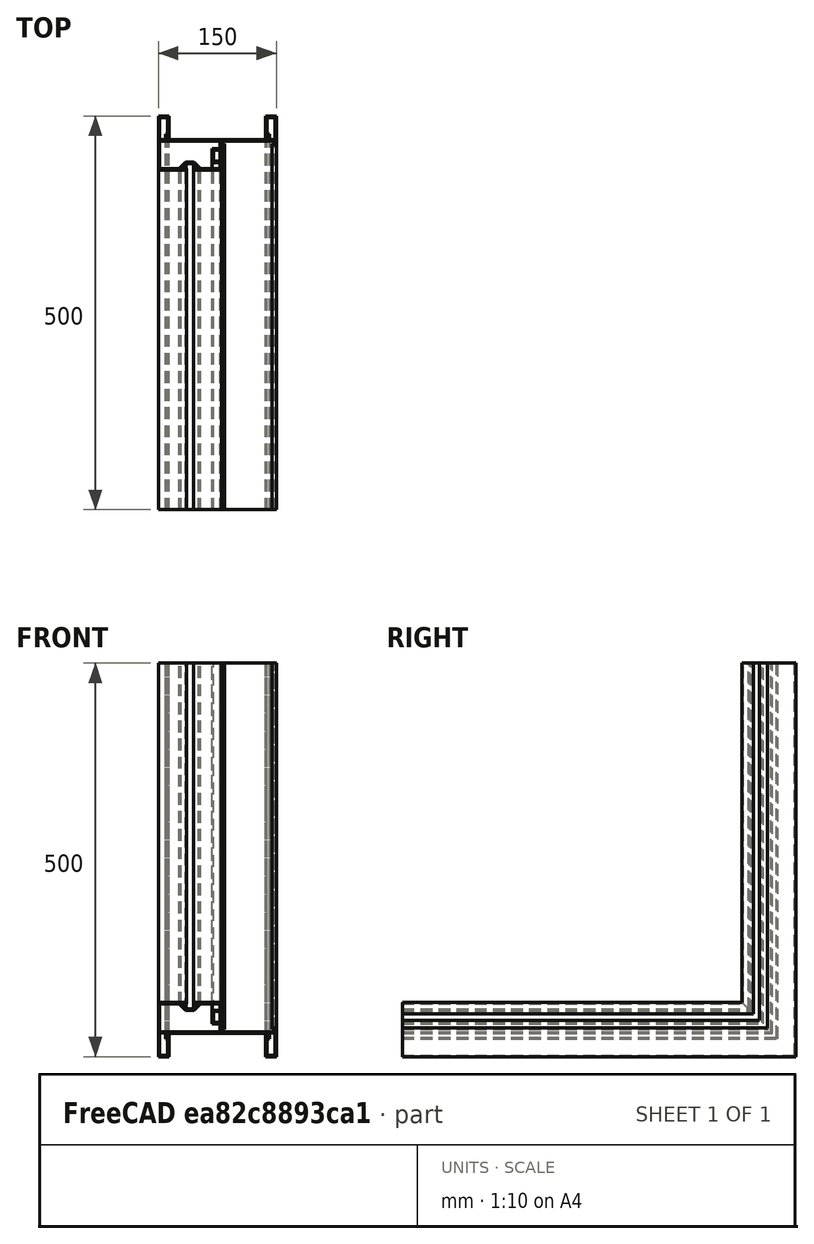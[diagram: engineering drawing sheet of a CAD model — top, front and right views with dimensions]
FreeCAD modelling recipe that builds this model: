
FCSTD DOCUMENT  (FreeCAD 0.20R24893 (Git))
Label: Profile_stripped
License: All rights reserved
LicenseURL: http://en.wikipedia.org/wiki/All_rights_reserved
objects: Part::Feature×5, Part::FeaturePython×4, Part::Face×1, Part::Extrusion×1, Fem::FemSolverObjectPython×1, App::MaterialObjectPython×1, PartDesign::Plane×1, Fem::ConstraintFixed×1, Fem::ConstraintForce×1, Part::MultiFuse×1, Fem::FemMeshObjectPython×1, Fem::FemAnalysis×1
note: 13 computed .brp shape members not serialized (recipe doc carries the construction recipe); baked Part::Feature solids carry a one-line shape summary decoded from their .brp

FEATURE [Part::Feature] Shape
  shape: bbox 150 x 68.8 x 2e-07 mm, 0 faces, 0 solids (baked)
FEATURE [Part::Feature] Shape001
  shape: bbox 10.2 x 28.2 x 2e-07 mm, 0 faces, 0 solids (baked)
FEATURE [Part::Feature] Shape002
  shape: bbox 76.4 x 35.2 x 2e-07 mm, 0 faces, 0 solids (baked)
FEATURE [Part::Feature] Shape003
  shape: bbox 10.2 x 28.2 x 2e-07 mm, 0 faces, 0 solids (baked)
FEATURE [Part::Face] Face
  FaceMakerClass = Part::FaceMakerBullseye
  Sources = -> [Shape003,Shape002,Shape001,Shape]
FEATURE [Part::Extrusion] Extrude
  Base = -> Face
  Dir = (0,0,1)
  DirMode = 2
  FaceMakerClass = Part::FaceMakerBullseye
  LengthFwd = 500
  LengthRev = 0
  Placement = pos=(0,-68.8,0) rot=(0,0,1;0rad)
  Solid = false
  Symmetric = false
FEATURE [Fem::FemSolverObjectPython] SolverCcxTools  # FEM object (typed FeaturePython)
  AnalysisType = 0
  BeamShellResultOutput3D = false
  EigenmodeHighLimit = 1000000
  EigenmodeLowLimit = 0
  EigenmodesCount = 10
  GeometricalNonlinearity = 0
  IterationsControlParameterCutb = 0.25,0.5,0.75,0.85,,,1.5,
  IterationsControlParameterIter = 4,8,9,200,10,400,,200,,
  IterationsControlParameterTimeUse = false
  IterationsThermoMechMaximum = 2000
  IterationsUserDefinedIncrementations = false
  IterationsUserDefinedTimeStepLength = false
  MaterialNonlinearity = 0
  MatrixSolverType = 0
  SplitInputWriter = false
  ThermoMechSteadyState = true
  TimeEnd = 1
  TimeInitialStep = 0.01
FEATURE [App::MaterialObjectPython] MaterialSolid  # material (typed FeaturePython)
  Category = 0
  Material = AuthorAndLicense=CalculiX-Steel,CardName=CalculiX-Steel,Density=7900 kg/m^3,Description=Standard steel material for CalculiX sample calculations,+7 more (map truncated)
FEATURE [Part::Feature] Extrude001  label="ExtrudeCopy"
  Placement = pos=(0,-500,68.8) rot=(-1,0,0;1.5708rad)
  shape: bbox 150 x 500 x 68.8 mm, 64 faces (baked)
FEATURE [PartDesign::Plane] PartDesign__Plane002
  AttachmentOffset = pos=(0,0,0) rot=(-1,0,0;0.785398rad)
  Length = 259.59
  MapMode = 49
  Placement = pos=(0,1.53e-14,3.411e-13) rot=(-1,0,0;0.785398rad)
  ResizeMode = 0
  Support = -> [Extrude001]
  Width = 838.26
FEATURE [Part::FeaturePython] Slice002  # WARN: FeaturePython — macro-defined, semantics opaque (R4)
  Base = -> Extrude001
  Mode = 1
  Tolerance = 0
  Tools = -> [PartDesign__Plane002]
FEATURE [Part::FeaturePython] Slice002_child0  label="Slice002.0"  # WARN: FeaturePython — macro-defined, semantics opaque (R4)
  Base = -> Slice002
  FilterType = 1
  Invert = false
  OverrideMaxVal = 0
  WindowFrom = 80
  WindowTo = 100
  items = 0
FEATURE [Fem::ConstraintFixed] ConstraintFixed
  NormalDirection = (-1,0,0)
  Normals = (13) [(-1,0,0),(-1,0,0),(-1,0,0),(-1,0,0),(-1,0,0),(-1,0,0),(-1,0,0),(-1,0,0),(-1,0,0),(-1,0,0),(-1,0,0),(-1,0,0),(-1,0,0)]
  Points = (13) [(0,0,2.27374e-13),(0,-166.667,68.8),(0,-166.667,45.8667),(0,-166.667,22.9333),(0,-166.667,2.27374e-13),(0,-333.333,68.8),(0,-333.333,45.8667),+6 more]
  References = -> [Slice002_child0]
  Scale = 18
FEATURE [Part::FeaturePython] Slice003  # WARN: FeaturePython — macro-defined, semantics opaque (R4)
  Base = -> Extrude
  Mode = 1
  Tolerance = 0
  Tools = -> [PartDesign__Plane002]
FEATURE [Part::FeaturePython] Slice003_child0  label="Slice003.0"  # WARN: FeaturePython — macro-defined, semantics opaque (R4)
  Base = -> Slice003
  FilterType = 1
  Invert = false
  OverrideMaxVal = 0
  WindowFrom = 80
  WindowTo = 100
  items = 0
FEATURE [Fem::ConstraintForce] ConstraintForce
  DirectionVector = (0,1,0)
  Force = 100
  NormalDirection = (0,-1,0)
  Points = (16) [(148.2,-31.8,500),(125.467,-31.8,500),(102.733,-31.8,500),(80,-31.8,500),(148.2,-31.8,343.933),(125.467,-31.8,343.933),(102.733,-31.8,343.933),+9 more]
  References = -> [Slice003_child0]
  Reversed = true
  Scale = 17
FEATURE [Part::MultiFuse] Fusion
  Refine = true
  Shapes = -> [Slice003_child0,Slice002_child0]
FEATURE [Fem::FemMeshObjectPython] FEMMeshGmsh  # FEM object (typed FeaturePython)
  Algorithm2D = 0
  Algorithm3D = 0
  CharacteristicLengthMax = 4
  CharacteristicLengthMin = 0
  CoherenceMesh = true
  ElementDimension = 3
  ElementOrder = 1
  GeometryTolerance = 0
  GroupsOfNodes = true
  HighOrderOptimize = 1
  MeshSizeFromCurvature = 12
  OptimizeNetgen = false
  OptimizeStd = true
  Part = -> Fusion
  RecombinationAlgorithm = 0
  Recombine3DAll = false
  RecombineAll = false
  SecondOrderLinear = false
FEATURE [Fem::FemAnalysis] Analysis
  Group = -> [SolverCcxTools,FEMMeshGmsh,ConstraintForce,ConstraintFixed,MaterialSolid]
